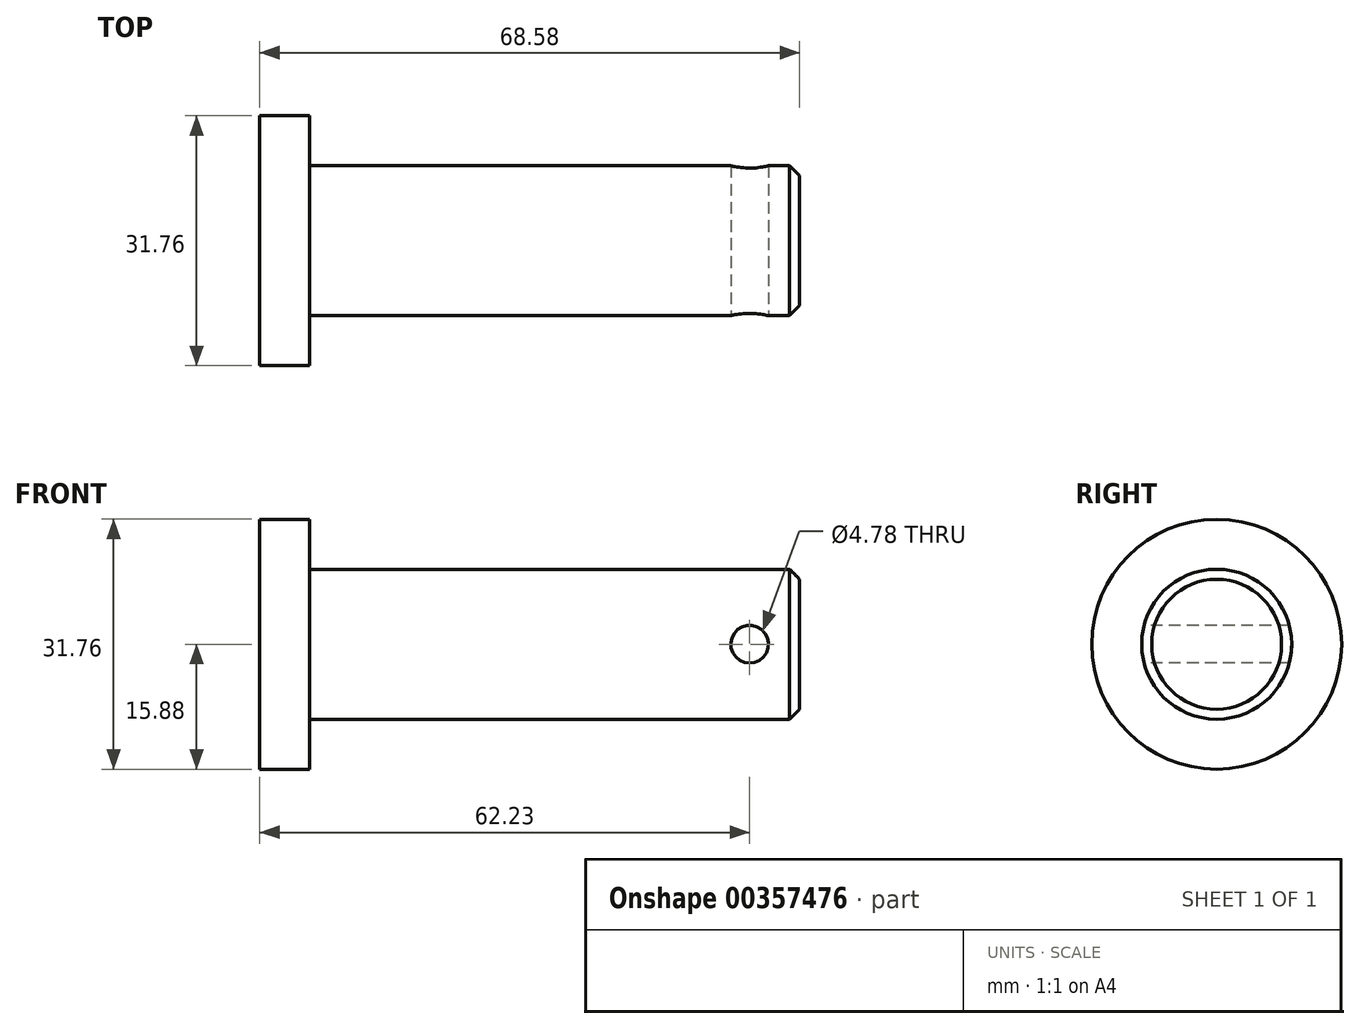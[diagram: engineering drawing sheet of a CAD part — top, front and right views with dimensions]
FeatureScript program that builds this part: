
annotation { "Feature Type Name" : "Feature", "Feature Type Description" : "" }
export const myFeature = defineFeature(function(context is Context, id is Id, definition is map)
    precondition{}
    {
        {
            var Q0;
            Q0=qCreatedBy(makeId("Front.planeOp"),FACE);
            var sketch = newSketch(context, id + "F0", { "sketchPlane" : qUnion([Q0])});
            skLineSegment(sketch, "E0", {"start": v(0, 0) * mm, "end": v(0, 15.88) * mm});
            skLineSegment(sketch, "E1", {"start": v(0, 15.88) * mm, "end": v(6.35, 15.88) * mm});
            skLineSegment(sketch, "E2", {"start": v(6.35, 9.52) * mm, "end": v(68.58, 9.52) * mm});
            skLineSegment(sketch, "E3", {"start": v(68.58, 9.53) * mm, "end": v(68.58, 0) * mm});
            skLineSegment(sketch, "E4", {"start": v(68.58, 0) * mm, "end": v(0, 0) * mm});
            skLineSegment(sketch, "E5", {"start": v(6.35, 15.88) * mm, "end": v(6.35, 0) * mm});
            skPoint(sketch, "E6", {"position": v(6.35, 7.94) * mm});
            skSolve(sketch);
        }
        {
            var Q0;
            {var subQ4=sQuery(id+"F0.wireOp",EDGE,"E0");Q0=makeQuery(id+"F0.imprint","IMPRINT",FACE,{"disambiguationData":[TD([[makeQuery(id+"F0.imprint","IMPRINT",EDGE,{"derivedFrom":subQ4}),-1.0]])]});}
            var Q1;
            {var subQ5=sQuery(id+"F0.wireOp",EDGE,"E2");Q1=makeQuery(id+"F0.imprint","IMPRINT",FACE,{"disambiguationData":[TD([[makeQuery(id+"F0.imprint","IMPRINT",EDGE,{"derivedFrom":subQ5}),-1.0]])]});}
            var Q2;
            Q2=sQuery(id+"F0.wireOp",EDGE,"E4");
            revolve(context, id + "F1", {"entities" : qUnion([Q0, Q1]), "axis" : qUnion([Q2]), "revolveType" : RevolveType.FULL});
        }
        {
            var Q0;
            Q0=qCreatedBy(makeId("Front.planeOp"),FACE);
            var sketch = newSketch(context, id + "F2", { "sketchPlane" : qUnion([Q0])});
            skCircle(sketch, "E7", {"center": v(62.23, 0) * mm, "radius": 2.39 * mm});
            skSolve(sketch);
        }
        {
            var Q0;
            Q0 = qSketchRegion(id + "F2", true);
            var Q1;
            Q1=sQuery(id+"F2.wireOp",EDGE,"E7");
            extrude(context, id + "F3", {"entities" : qUnion([Q0]), "operationType" : NewBodyOperationType.REMOVE, "surfaceEntities" : qUnion([Q1]), "oppositeDirection" : true, "depth" : 25.4 * mm, "hasSecondDirection" : true, "secondDirectionOppositeDirection" : false, "secondDirectionDepth" : 25.4 * mm});
        }
        {
            var Q0;
            Q0=makeQuery(id+"F1.opRevolve","SWEPT_EDGE",EDGE,{"disambiguationData":[OSD([sQuery(id+"F0.wireOp",EDGE,"E2"),sQuery(id+"F0.wireOp",EDGE,"E3")])]});
            chamfer(context, id + "F4", {"entities" : qUnion([Q0]), "chamferType" : ChamferType.OFFSET_ANGLE, "width" : 1.27 * mm, "oppositeDirection" : false, "angle" : 45 * degree, "tangentPropagation" : true});
        }
    });
